# Revit family: IS_LDV_E2713_BIM_GB
name_source: partatom
category: Plumbing Fixtures
units: mm (PartAtom-declared; Revit-internal decimal feet)

## family parameters
Cut with Voids When Loaded = No
Host = Face
Maintain Annotation Orientation = No
OmniClass Number = 23.45.05.21.11.11
OmniClass Title = Water Operated Water Closets
Part Type = Normal
Room Calculation Point = No
Round Connector Dimension = Use Diameter
Shared = Yes

## types (1)
- E271301 - LDV CIST SI 6/3 CC WHT BXD
    Accessories = https://www.idealstandard.co.uk
    AreaUnits = millimeters
    Assembly Code = C1030200
    AssetType = Fixed
    BIMObjectName = IS_LDV_Cistern_E2713
    BREEAMApproved = No
    BarCode = 5017830562610
    Brand = Ideal Standard
    CWFU = 0
    ConnectionType = Plumbing
    Cost = 0 $
    Default Elevation = 0 mm  [stored 0 ft]
    Description = La Dolce Vita® cistern, side inlet, trim mounted, pre-adjusted, 6/3 l, white
    DurationUnit = year
    ECA = No
    EPD = https://www.idealstandard.co.uk
    ExpectedLife = 30
    Features = La Dolce Vita® cistern, side inlet, trim mounted, pre-adjusted, 6/3 l, white, carton box, EU pallet
    Finish = white
    HWFU = 0
    Help = https://www.idealstandard.co.uk
    IfcExportAs = IfcSanitaryTerminalType
    IfcExportType = CISTERN
    InstallationInstructions = https://www.idealstandard.co.uk
    LinearUnits = millimeters
    Manufacturer = Ideal Standard
    ManufacturerURL = https://www.idealstandard.co.uk
    Model = E271301
    ModelNumber = E271301
    ModelReference = La Dolce Vita® cistern, side inlet, trim mounted, pre-adjusted, 6/3 l, white
    NBSDescription = WC cisterns
    NBSReference = Pr_40_20_93_89
    Name = Cistern_LDV_E2713_IdealStandard
    NettWeight = 12
    NominalDepth = 148 mm
    NominalHeight = 388 mm
    NominalLength = 148 mm
    NominalWidth = 372 mm
    ProductInformation = https://www.idealstandard.co.uk
    Shape = Sculptured
    Size = 372 x 148 x 388 mm
    Space = Internal
    SpilloverLevel = 0 mm  [stored 0 ft]
    ToiletPanType = WashDown
    ToiletType = Other
    URL = https://www.idealstandard.co.uk
    Uniclass2015Code = Pr_40_20_93_89
    Uniclass2015Description = WC cisterns
    Uniclass2015Title = WC cisterns
    Uniclass2015Version = Products v1.33
    Version = 1
    VolumeUnits = Litres
    WFU = 0
    WRAS = No
    WarrantyDescription = Manufacturers Warranty
    WarrantyDurationParts = 0
    WarrantyDurationUnit = year
    WarrantyGuarantorParts = Ideal Standard
    WaterEfficientProduct = No

note: [stored X ft] marks values corroborated as IEEE doubles in the binary element streams (Revit-internal decimal feet)

## geometry (parser evidence)
native form markers: Sweep x2
no freeform markers — native parametric forms only
